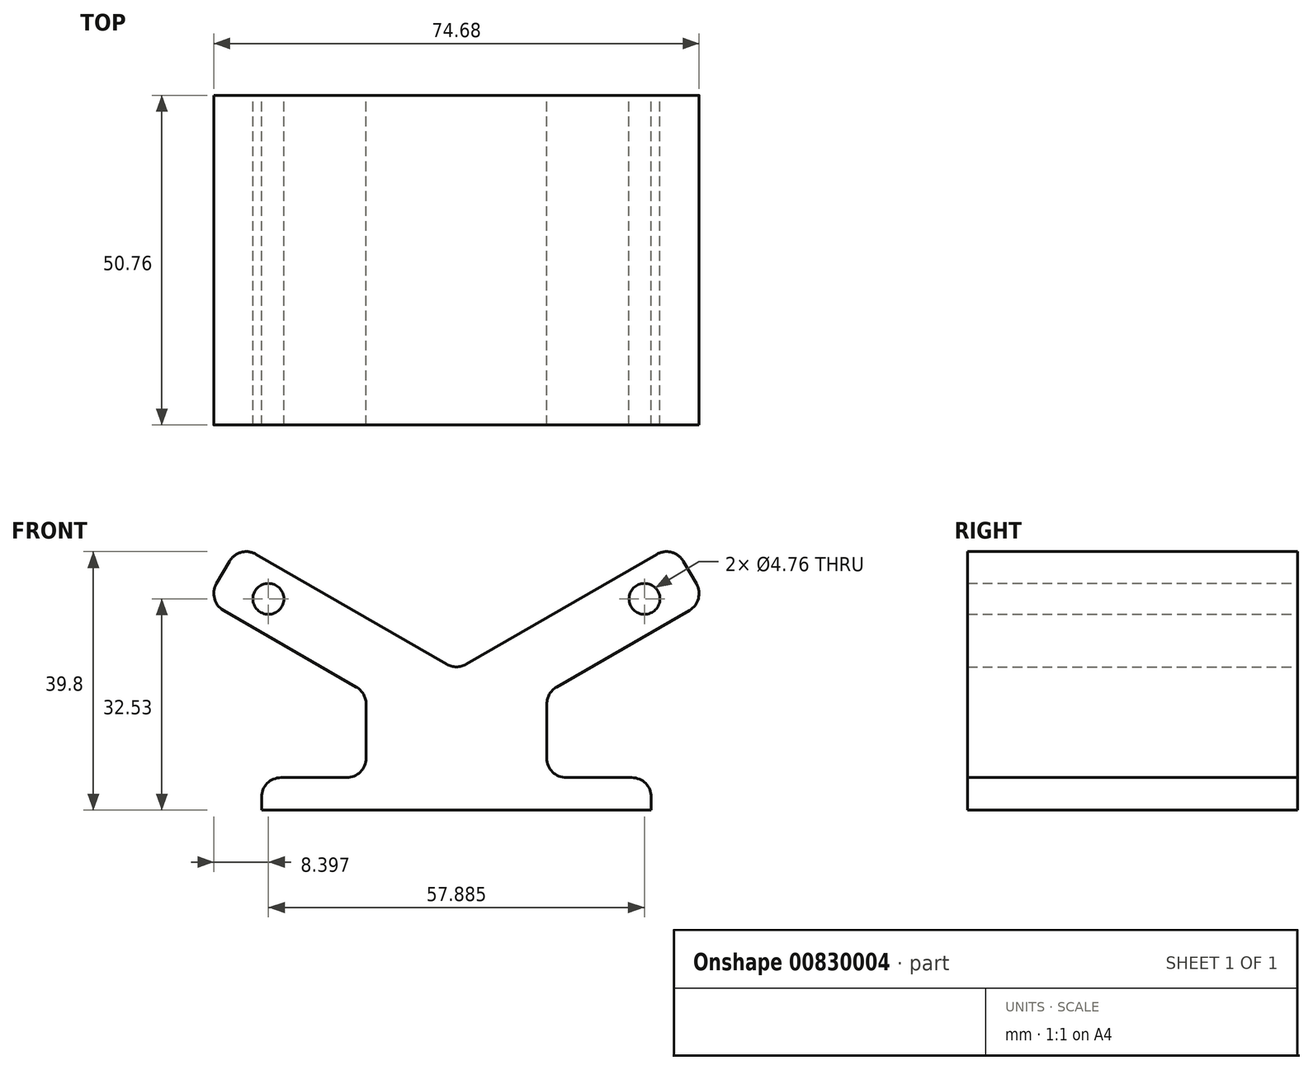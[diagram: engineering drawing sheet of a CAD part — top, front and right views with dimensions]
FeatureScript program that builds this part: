
annotation { "Feature Type Name" : "Feature", "Feature Type Description" : "" }
export const myFeature = defineFeature(function(context is Context, id is Id, definition is map)
    precondition{}
    {
        {
            var Q0;
            Q0=qCreatedBy(makeId("Front.planeOp"),FACE);
            var sketch = newSketch(context, id + "F0", { "sketchPlane" : qUnion([Q0])});
            skCircle(sketch, "E0", {"center": v(0, 0) * mm, "radius": 15.82 * mm, "construction": true});
            skLineSegment(sketch, "E1", {"start": v(0, 0) * mm, "end": v(0, 15.82) * mm, "construction": true});
            skLineSegment(sketch, "E2.1.0", {"start": v(0, 0) * mm, "end": v(-43.65, -25.2) * mm, "construction": true});
            skLineSegment(sketch, "E2.2.0", {"start": v(0, 0) * mm, "end": v(47.18, -27.24) * mm, "construction": true});
            skPoint(sketch, "E3.orphan", {"position": v(-13.7, -7.9) * mm});
            skPoint(sketch, "E4.orphan", {"position": v(13.7, -7.91) * mm});
            skCircle(sketch, "E5", {"center": v(-28.94, -16.7) * mm, "radius": 17.6 * mm, "construction": true});
            skCircle(sketch, "E6", {"center": v(28.94, -16.7) * mm, "radius": 17.6 * mm, "construction": true});
            skCircle(sketch, "E7", {"center": v(-28.94, -16.7) * mm, "radius": 2.38 * mm});
            skCircle(sketch, "E8", {"center": v(28.94, -16.7) * mm, "radius": 2.38 * mm});
            skLineSegment(sketch, "E9", {"start": v(-28.94, -16.7) * mm, "end": v(28.94, -16.7) * mm, "construction": true});
            skCircle(sketch, "E10.MirrorC", {"center": v(0, -33.42) * mm, "radius": 15.82 * mm, "construction": true});
            skLineSegment(sketch, "E11", {"start": v(30, -49.24) * mm, "end": v(-30, -49.24) * mm});
            skPoint(sketch, "E12", {"position": v(0, -49.24) * mm});
            skLineSegment(sketch, "E13.bottom", {"start": v(-13.91, -49.24) * mm, "end": v(13.91, -49.24) * mm});
            skLineSegment(sketch, "E13.top", {"start": v(-13.91, -17.6) * mm, "end": v(-11.37, -17.6) * mm});
            skLineSegment(sketch, "E13.left", {"start": v(-13.91, -44.24) * mm, "end": v(-13.91, -31.16) * mm});
            skLineSegment(sketch, "E13.right", {"start": v(13.91, -44.24) * mm, "end": v(13.91, -31.16) * mm});
            skLineSegment(sketch, "E14.bottom", {"start": v(-30, -49.24) * mm, "end": v(30, -49.24) * mm});
            skLineSegment(sketch, "E14.top", {"start": v(-30, -44.24) * mm, "end": v(-13.91, -44.24) * mm});
            skLineSegment(sketch, "E14.left", {"start": v(-30, -49.24) * mm, "end": v(-30, -44.24) * mm});
            skLineSegment(sketch, "E14.right", {"start": v(30, -49.24) * mm, "end": v(30, -44.24) * mm});
            skLineSegment(sketch, "E15", {"start": v(0, -33.42) * mm, "end": v(-28.94, -16.7) * mm, "construction": true});
            skLineSegment(sketch, "E16", {"start": v(0, -33.42) * mm, "end": v(28.94, -16.7) * mm, "construction": true});
            skLineSegment(sketch, "E17", {"start": v(-13.91, -31.16) * mm, "end": v(-38.44, -17) * mm});
            skLineSegment(sketch, "E18", {"start": v(0, -49.24) * mm, "end": v(0, 31.7) * mm, "construction": true});
            skLineSegment(sketch, "E19.MirrorCS", {"start": v(0, -27.65) * mm, "end": v(-33.44, -8.34) * mm});
            skLineSegment(sketch, "E20.MirrorCS", {"start": v(0, -27.65) * mm, "end": v(33.44, -8.34) * mm});
            skLineSegment(sketch, "E21.MirrorCS", {"start": v(13.91, -31.16) * mm, "end": v(38.44, -17) * mm});
            skLineSegment(sketch, "E22", {"start": v(-38.44, -17) * mm, "end": v(-33.44, -8.34) * mm});
            skLineSegment(sketch, "E23", {"start": v(38.44, -17) * mm, "end": v(33.44, -8.34) * mm});
            skPoint(sketch, "E24.orphan", {"position": v(-5, -30.53) * mm});
            skPoint(sketch, "E25.orphan", {"position": v(5, -30.53) * mm});
            skPoint(sketch, "E26.trimOffspring.end.orphan", {"position": v(13.91, -17.6) * mm});
            skLineSegment(sketch, "E27.trimOffspring", {"start": v(-13.91, -25.89) * mm, "end": v(-13.91, -25.39) * mm});
            skPoint(sketch, "E28.orphan", {"position": v(0, -39.2) * mm});
            skLineSegment(sketch, "E29.trimOffspring", {"start": v(13.91, -25.89) * mm, "end": v(13.91, -25.39) * mm});
            skLineSegment(sketch, "E30.trimOffspring", {"start": v(13.91, -44.24) * mm, "end": v(30, -44.24) * mm});
            skSolve(sketch);
        }
        {
            var Q0;
            Q0=makeQuery(id+"F0.imprint","IMPRINT",FACE,{"disambiguationData":[TD([[makeQuery(id+"F0.imprint","IMPRINT",EDGE,{"derivedFrom":sQuery(id+"F0.wireOp",EDGE,"E7")}),-1.0]])]});
            extrude(context, id + "F1", {"entities" : qUnion([Q0]), "depth" : 50.76 * mm, "offsetDistance" : 25 * mm});
        }
        {
            var Q0;
            Q0=makeQuery(id+"F1.opExtrude","SWEPT_EDGE",EDGE,{"disambiguationData":[OSD([sQuery(id+"F0.wireOp",EDGE,"E19.MirrorCS"),sQuery(id+"F0.wireOp",EDGE,"E22")])]});
            var Q1;
            Q1=makeQuery(id+"F1.opExtrude","SWEPT_EDGE",EDGE,{"disambiguationData":[OSD([sQuery(id+"F0.wireOp",EDGE,"E17"),sQuery(id+"F0.wireOp",EDGE,"E22")])]});
            var Q2;
            Q2=makeQuery(id+"F1.opExtrude","SWEPT_EDGE",EDGE,{"disambiguationData":[OSD([sQuery(id+"F0.wireOp",EDGE,"E19.MirrorCS"),sQuery(id+"F0.wireOp",EDGE,"E20.MirrorCS")])]});
            var Q3;
            Q3=makeQuery(id+"F1.opExtrude","SWEPT_EDGE",EDGE,{"disambiguationData":[OSD([sQuery(id+"F0.wireOp",EDGE,"E20.MirrorCS"),sQuery(id+"F0.wireOp",EDGE,"E23")])]});
            var Q4;
            Q4=makeQuery(id+"F1.opExtrude","SWEPT_EDGE",EDGE,{"disambiguationData":[OSD([sQuery(id+"F0.wireOp",EDGE,"E21.MirrorCS"),sQuery(id+"F0.wireOp",EDGE,"E23")])]});
            var Q5;
            Q5=makeQuery(id+"F1.opExtrude","SWEPT_EDGE",EDGE,{"disambiguationData":[OSD([sQuery(id+"F0.wireOp",EDGE,"E13.right"),sQuery(id+"F0.wireOp",EDGE,"E21.MirrorCS")])]});
            var Q6;
            Q6=makeQuery(id+"F1.opExtrude","SWEPT_EDGE",EDGE,{"disambiguationData":[OSD([sQuery(id+"F0.wireOp",EDGE,"E13.right"),sQuery(id+"F0.wireOp",EDGE,"E30.trimOffspring")])]});
            var Q7;
            Q7=makeQuery(id+"F1.opExtrude","SWEPT_EDGE",EDGE,{"disambiguationData":[OSD([sQuery(id+"F0.wireOp",EDGE,"E13.left"),sQuery(id+"F0.wireOp",EDGE,"E17")])]});
            var Q8;
            Q8=makeQuery(id+"F1.opExtrude","SWEPT_EDGE",EDGE,{"disambiguationData":[OSD([sQuery(id+"F0.wireOp",EDGE,"E13.left"),sQuery(id+"F0.wireOp",EDGE,"E14.top")])]});
            var Q9;
            Q9=makeQuery(id+"F1.opExtrude","SWEPT_EDGE",EDGE,{"disambiguationData":[OSD([sQuery(id+"F0.wireOp",EDGE,"E14.top"),sQuery(id+"F0.wireOp",EDGE,"E14.left")])]});
            var Q10;
            Q10=makeQuery(id+"F1.opExtrude","SWEPT_EDGE",EDGE,{"disambiguationData":[OSD([sQuery(id+"F0.wireOp",EDGE,"E14.right"),sQuery(id+"F0.wireOp",EDGE,"E30.trimOffspring")])]});
            fillet(context, id + "F2", {"entities" : qUnion([Q0, Q1, Q2, Q3, Q4, Q5, Q6, Q7, Q8, Q9, Q10]), "radius" : 3 * mm, "tangentPropagation" : true, "allowEdgeOverflow" : false});
        }
    });
